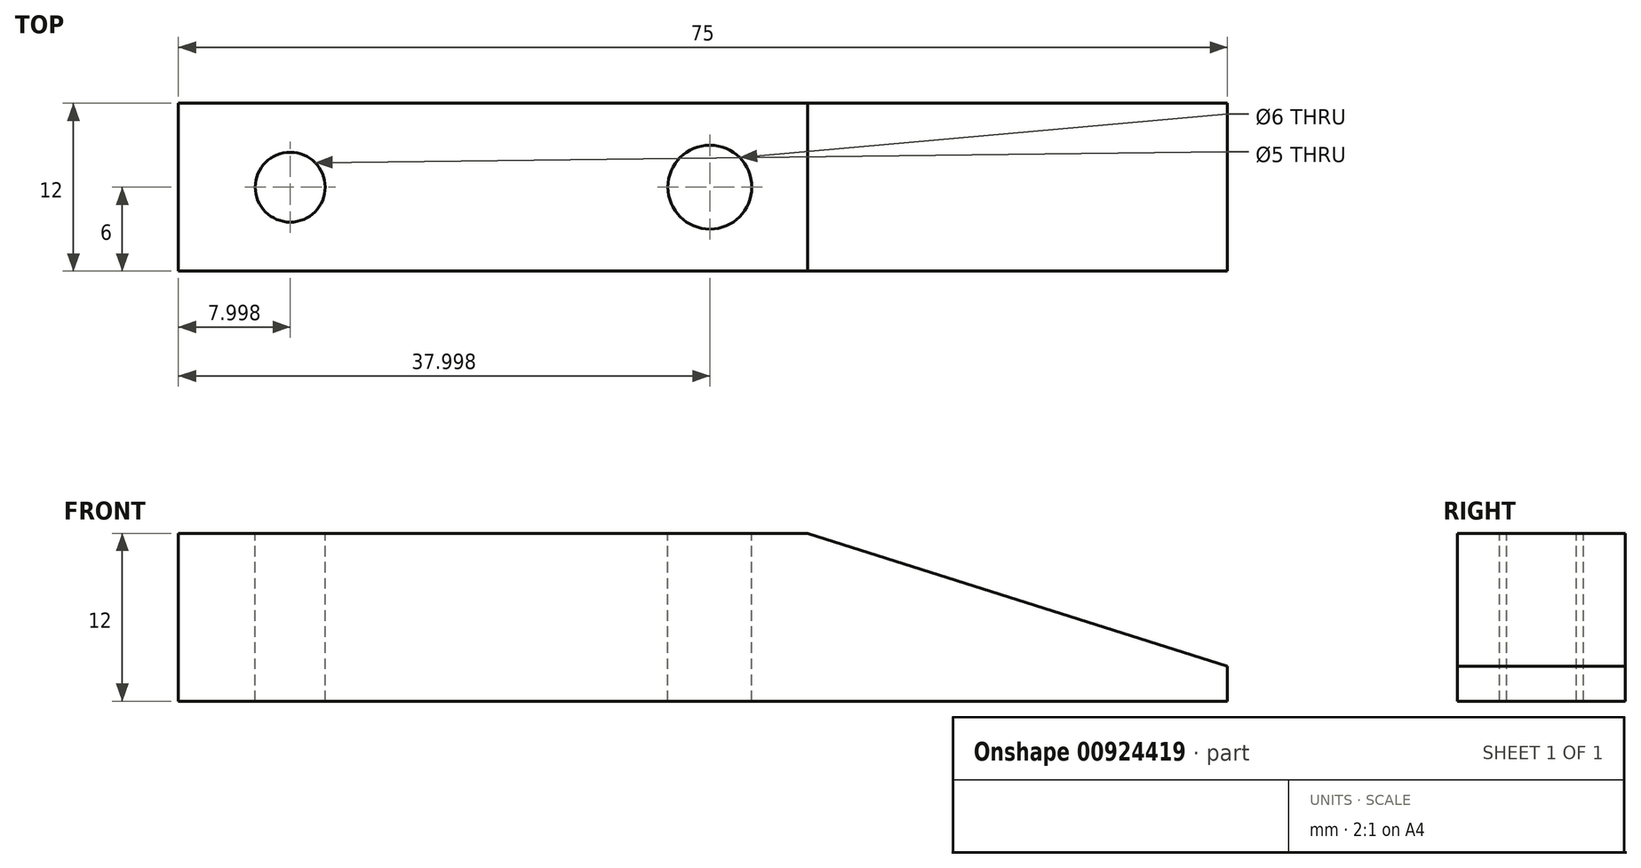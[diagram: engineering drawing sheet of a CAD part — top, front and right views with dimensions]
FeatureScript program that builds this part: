
annotation { "Feature Type Name" : "Feature", "Feature Type Description" : "" }
export const myFeature = defineFeature(function(context is Context, id is Id, definition is map)
    precondition{}
    {
        {
            var Q0;
            Q0=qCreatedBy(makeId("Front.planeOp"),FACE);
            var sketch = newSketch(context, id + "F0", { "sketchPlane" : qUnion([Q0])});
            skLineSegment(sketch, "E0", {"start": v(-24.53, 11.38) * mm, "end": v(20.47, 11.38) * mm});
            skLineSegment(sketch, "E1", {"start": v(20.47, 11.38) * mm, "end": v(50.47, 1.88) * mm});
            skLineSegment(sketch, "E2", {"start": v(50.47, 1.88) * mm, "end": v(50.47, -0.62) * mm});
            skLineSegment(sketch, "E3", {"start": v(50.47, -0.62) * mm, "end": v(-24.53, -0.62) * mm});
            skLineSegment(sketch, "E4", {"start": v(-24.53, -0.62) * mm, "end": v(-24.53, 11.38) * mm});
            skSolve(sketch);
        }
        {
            var Q0;
            Q0 = qSketchRegion(id + "F0", true);
            extrude(context, id + "F1", {"entities" : qUnion([Q0]), "depth" : 12 * mm, "offsetDistance" : 25 * mm});
        }
        {
            var Q0;
            Q0=makeQuery(id+"F1.opExtrude","SWEPT_FACE",FACE,{"disambiguationData":[OSD([sQuery(id+"F0.wireOp",EDGE,"E0")])]});
            var sketch = newSketch(context, id + "F2", { "sketchPlane" : qUnion([Q0])});
            skCircle(sketch, "E5", {"center": v(-16.53, -6) * mm, "radius": 2.5 * mm});
            skCircle(sketch, "E6", {"center": v(13.47, -6) * mm, "radius": 3 * mm});
            skSolve(sketch);
        }
        {
            var Q0;
            Q0 = qSketchRegion(id + "F2", true);
            extrude(context, id + "F3", {"entities" : qUnion([Q0]), "operationType" : NewBodyOperationType.REMOVE, "oppositeDirection" : true, "depth" : 25 * mm, "offsetDistance" : 25 * mm});
        }
    });
